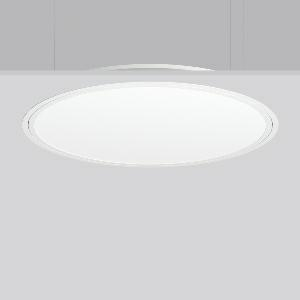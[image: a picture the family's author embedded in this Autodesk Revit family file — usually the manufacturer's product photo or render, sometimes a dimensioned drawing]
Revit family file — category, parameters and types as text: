
# Revit family: triona_round_e_312387_002_2_12_7e8f
name_source: partatom
category: Lighting Fixtures
units: mm (PartAtom-declared; Revit-internal decimal feet)

## family parameters
Cut with Voids When Loaded = No
Host = Face
Light Source = No
Part Type = Normal
Room Calculation Point = No
Round Connector Dimension = Use Diameter
Shared = No

## types (1)
- TuneableWhite 846 (1 x LED Modul 846, 4800 lm, 4600)
    Apparent Load = 49 VA
    CIE Flux Codes = 50 80 96 100 100
    Color Rendering = 80
    Color Temperature = 4600
    Default Elevation = 1800 mm
    Description = Series: TRIONA round
Decorative round LED recessed surface luminaire. Cover made of sheet steel, powder-coated. Frame made of aluminium, powder-coated. Recessed ring: aluminium extrusion profile, powder coated. Light emission through a diffuser: plastic, opal. Lightguide and diffuser made of non-yellowing plastic (PMMA). Lateral light emission (RZB SIDELITE technology) for above-average homogeneous light distribution. Tunable white versions, dynamically adjustable from 2700 K to 6500 K. Suitable for installation in cavity ceilings. Tool-free mounting system thanks to the rocker arm mechanism (patent pending). Electronic ballast included. Very easy installation thanks to Plug+Play connection. Ideal for use as part of the Human Centric Lighting concept in connection with RZB light management systems. 
Colour: traffic white, matt (RAL 9016)
Diameter: 889 mm
Height: 2 mm
Cut-out diameter: 866 mm
Recess height: 100 mm
Luminaire: recess height: 89 mm
Lamp: LED
Socket: without socket
Colour temperature: 2700K - 6500K
Colour rendering index (CRI): 80
System power: 49 W
Rated luminous flux: 4800 lm
Luminous efficiency: 98 lm/W
System power 2: 51 W
Rated luminous flux 2: 4550 lm
Luminous efficiency 2: 89 lm/W
System power 3: 51 W
Rated luminous flux 3: 4650 lm
Luminous efficiency 3: 91 lm/W
Control gear: Converter, dimmable, DALI
Protection class: I
Type of protection: IP 40
    Height = 0 mm  [stored 0 ft]
    Lamp = 1 x LED Modul 846
    Lamp Light Flux = 4800 lm
    Lamp count = 1
    Length = 889 mm
    Lifetime = 50000 h
    Luminous efficacy = 98 lm/W
    Manufacturer = RZB
    ModVariant = No
    Model = 312387.002.2.12
    Mounting Place = Ceiling
    Mounting Type = Recessed
    Number of Poles = 1
    OnlyDefault = Yes
    Power Factor = 1
    Product Name = TRIONA round E
    Product group = Recessed modular luminaires
    ProductGroupID = 406
    Protection Class = Protection class I
    Protection Degree = IP 20
    RLX_Detail_Level = 1
    RLX_Emergency_Light_Flux = 0 lm
    RLX_Emergency_Type = 0
    RLX_Emergency_Type_DB = No
    RlxData = <blob elided: 38213 chars, md5=c16fef11>
    Socket = socket
    Standby Power = 0 W
    System Light Flux = 4800 lm
    System Power = 49 W
    Type Comments = TuneableWhite 846
    Type Image = 312387.002.12.jpg
    URL = http://relux.com
    VarID = tuneablewhite_846
    Voltage = 230 V
    Voltage Range = 220-240 V
    Weight = 0.00 kg
    Width = 0 mm  [stored 0 ft]

note: [stored X ft] marks values corroborated as IEEE doubles in the binary element streams (Revit-internal decimal feet)

## geometry (parser evidence)
native form markers: Blend x4, Sweep x10
no freeform markers — native parametric forms only
